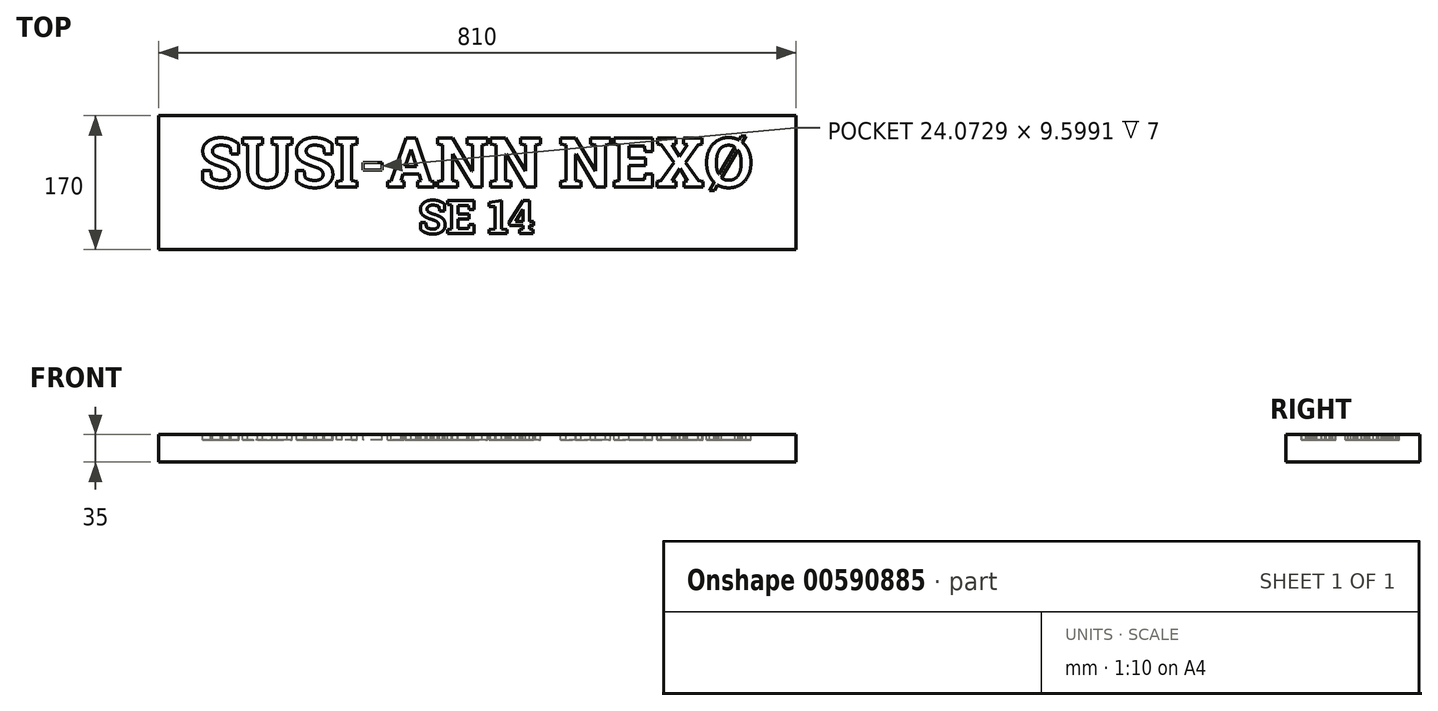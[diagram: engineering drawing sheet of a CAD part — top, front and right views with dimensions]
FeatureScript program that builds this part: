
annotation { "Feature Type Name" : "Feature", "Feature Type Description" : "" }
export const myFeature = defineFeature(function(context is Context, id is Id, definition is map)
    precondition{}
    {
        {
            var Q0;
            Q0=qCreatedBy(makeId("Top.planeOp"),FACE);
            var sketch = newSketch(context, id + "F0", { "sketchPlane" : qUnion([Q0])});
            skLineSegment(sketch, "E0.bottom", {"start": v(-405, 85) * mm, "end": v(405, 85) * mm});
            skLineSegment(sketch, "E0.top", {"start": v(-405, -85) * mm, "end": v(405, -85) * mm});
            skLineSegment(sketch, "E0.left", {"start": v(-405, 85) * mm, "end": v(-405, -85) * mm});
            skLineSegment(sketch, "E0.right", {"start": v(405, 85) * mm, "end": v(405, -85) * mm});
            skLineSegment(sketch, "E1", {"start": v(-405, 0) * mm, "end": v(405, 0) * mm, "construction": true});
            skLineSegment(sketch, "E2", {"start": v(0, -85) * mm, "end": v(0, 85) * mm, "construction": true});
            skLineSegment(sketch, "E3", {"start": v(0, 0) * mm, "end": v(0, 154.96) * mm, "construction": true});
            skSolve(sketch);
        }
        {
            var Q0;
            Q0 = qSketchRegion(id + "F0", true);
            extrude(context, id + "F1", {"entities" : qUnion([Q0]), "depth" : 35 * mm, "offsetDistance" : 25 * mm});
        }
        {
            var Q0;
            Q0=makeQuery(id+"F1.opExtrude","CAP_FACE",FACE,{"disambiguationData":[OSD([sQuery(id+"F0.wireOp",EDGE,"E0.bottom"),sQuery(id+"F0.wireOp",EDGE,"E0.top"),sQuery(id+"F0.wireOp",EDGE,"E0.left"),sQuery(id+"F0.wireOp",EDGE,"E0.right")])],"isStart":false});
            var sketch = newSketch(context, id + "F2", { "sketchPlane" : qUnion([Q0])});
            skText(sketch, "E4", { "text": "SUSI-ANN NEXØ", "fontName": "RobotoSlab-Bold.ttf"});
            skLineSegment(sketch, "E5", {"start": v(0, 81.83) * mm, "end": v(0, -81.83) * mm, "construction": true});
            skText(sketch, "E6", { "text": "SE 14", "fontName": "RobotoSlab-Bold.ttf"});
            const initialGuessF2  = {"E4": [-0.3529, -0.0057, 1, 0, 0.06292], "E6": [-0.07496, -0.06471, 1, 0, 0.04265]};
            skSetInitialGuess(sketch, initialGuessF2);
            skSolve(sketch);
        }
        {
            var Q0;
            Q0 = qSketchRegion(id + "F2", true);
            extrude(context, id + "F3", {"entities" : qUnion([Q0]), "operationType" : NewBodyOperationType.REMOVE, "oppositeDirection" : true, "depth" : 7 * mm, "offsetDistance" : 25 * mm});
        }
    });
